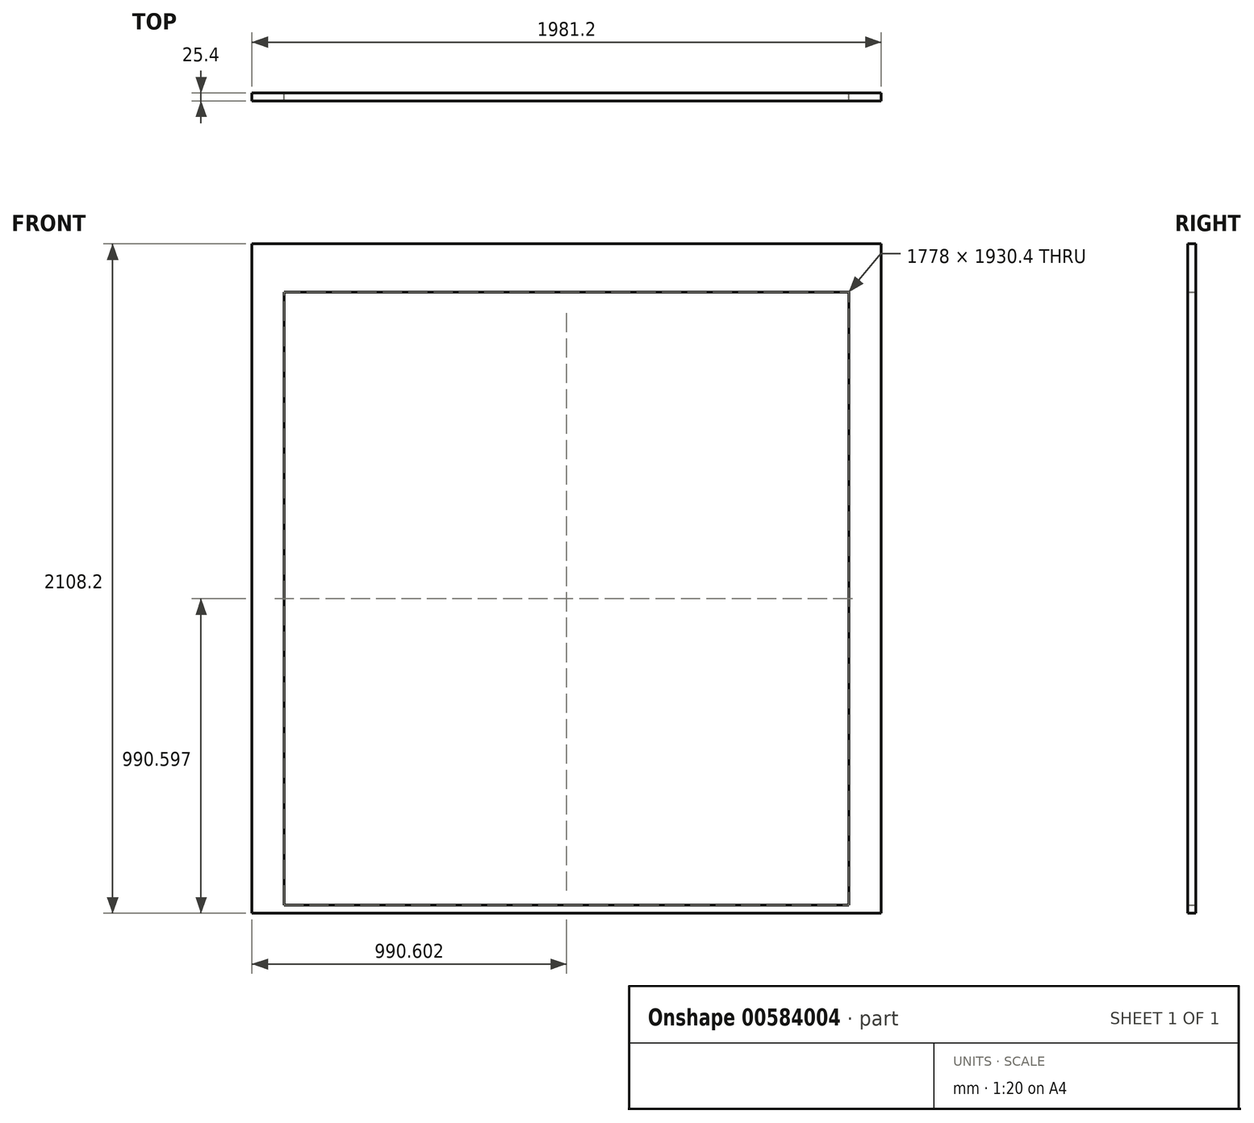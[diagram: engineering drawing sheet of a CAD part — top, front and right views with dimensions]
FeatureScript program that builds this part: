
annotation { "Feature Type Name" : "Feature", "Feature Type Description" : "" }
export const myFeature = defineFeature(function(context is Context, id is Id, definition is map)
    precondition{}
    {
        {
            var Q0;
            Q0=qCreatedBy(makeId("Front.planeOp"),FACE);
            var sketch = newSketch(context, id + "F0", { "sketchPlane" : qUnion([Q0])});
            skLineSegment(sketch, "E0.bottom", {"start": v(961.35, -896.76) * mm, "end": v(-1019.85, -896.76) * mm});
            skLineSegment(sketch, "E0.top", {"start": v(961.35, 1211.44) * mm, "end": v(-1019.85, 1211.44) * mm});
            skLineSegment(sketch, "E0.left", {"start": v(961.35, -896.76) * mm, "end": v(961.35, 1211.44) * mm});
            skLineSegment(sketch, "E0.right", {"start": v(-1019.85, -896.76) * mm, "end": v(-1019.85, 1211.44) * mm});
            skPoint(sketch, "E0.middle", {"position": v(-29.25, 157.34) * mm});
            skLineSegment(sketch, "E1.bottom", {"start": v(-918.25, 1059.04) * mm, "end": v(859.75, 1059.04) * mm});
            skLineSegment(sketch, "E1.top", {"start": v(-918.25, -871.36) * mm, "end": v(859.75, -871.36) * mm});
            skLineSegment(sketch, "E1.left", {"start": v(-918.25, 1059.04) * mm, "end": v(-918.25, -871.36) * mm});
            skLineSegment(sketch, "E1.right", {"start": v(859.75, 1059.04) * mm, "end": v(859.75, -871.36) * mm});
            skSolve(sketch);
        }
        {
            var Q0;
            Q0=makeQuery(id+"F0.imprint","IMPRINT",FACE,{"disambiguationData":[TD([[makeQuery(id+"F0.imprint","IMPRINT",EDGE,{"derivedFrom":sQuery(id+"F0.wireOp",EDGE,"E0.bottom")}),-1.0]])]});
            extrude(context, id + "F1", {"entities" : qUnion([Q0]), "depth" : 25.4 * mm, "offsetDistance" : 25.4 * mm});
        }
    });
